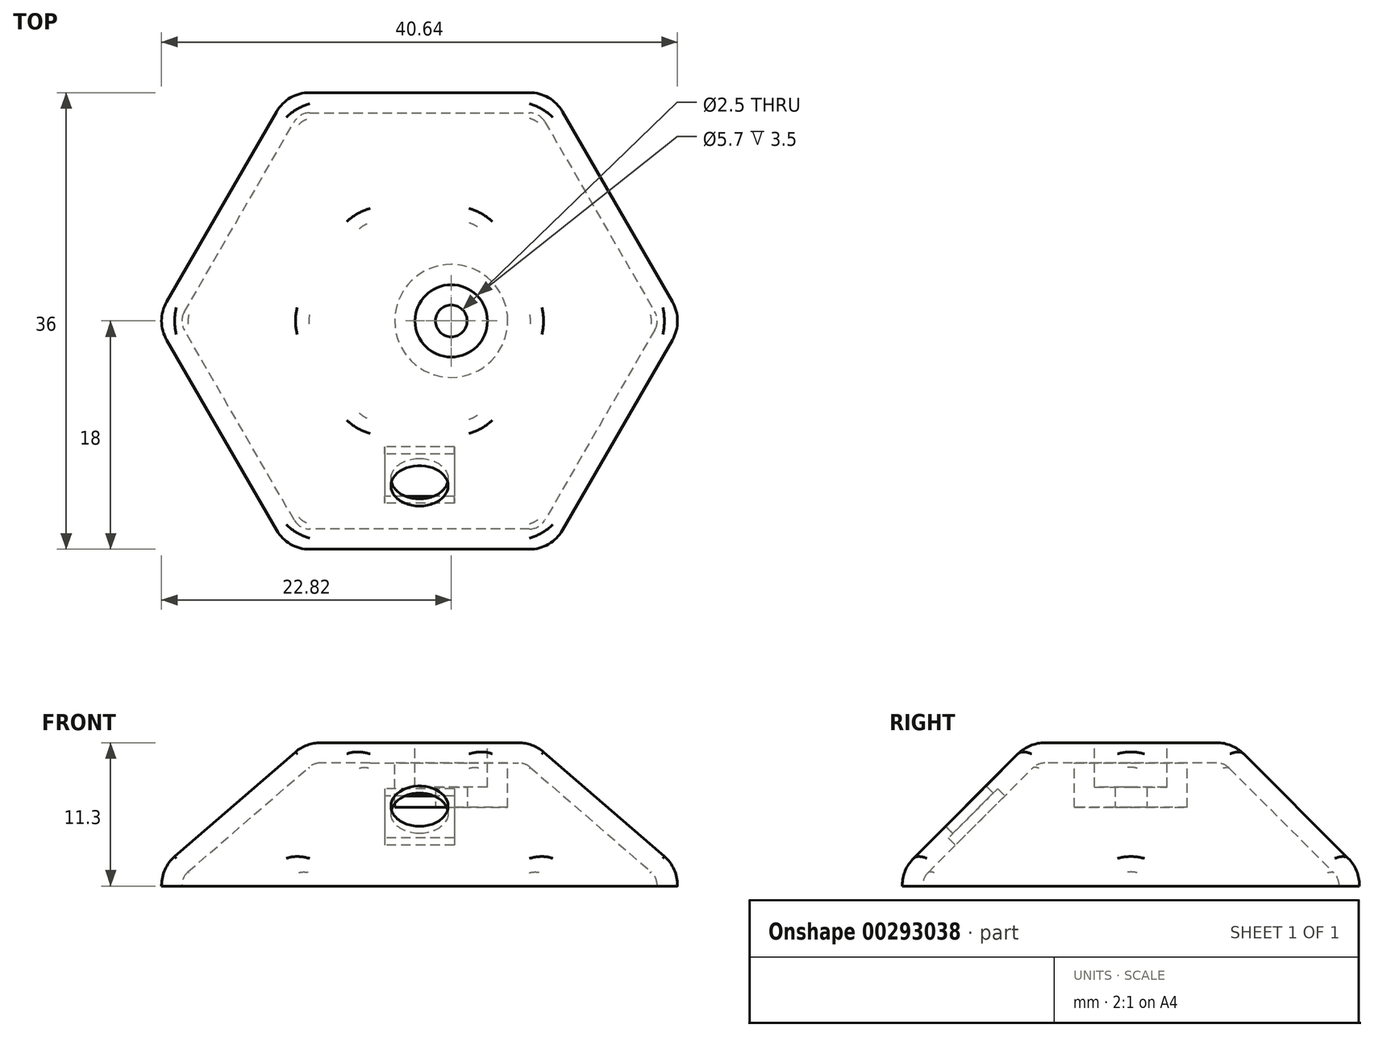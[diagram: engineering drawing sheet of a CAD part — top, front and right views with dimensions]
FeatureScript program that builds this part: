
annotation { "Feature Type Name" : "Feature", "Feature Type Description" : "" }
export const myFeature = defineFeature(function(context is Context, id is Id, definition is map)
    precondition{}
    {
        {
            var Q0;
            Q0=qCreatedBy(makeId("Top.planeOp"),FACE);
            var sketch = newSketch(context, id + "F0", { "sketchPlane" : qUnion([Q0])});
            skCircle(sketch, "E0.cCircle", {"center": v(0, 0) * mm, "radius": 18 * mm, "construction": true});
            skLineSegment(sketch, "E0.0", {"start": v(-10.4, 18) * mm, "end": v(10.4, 18) * mm});
            skLineSegment(sketch, "E0.1", {"start": v(10.4, 18) * mm, "end": v(20.78, 0) * mm});
            skLineSegment(sketch, "E0.2", {"start": v(20.78, 0) * mm, "end": v(10.4, -18) * mm});
            skLineSegment(sketch, "E0.3", {"start": v(10.4, -18) * mm, "end": v(-10.4, -18) * mm});
            skLineSegment(sketch, "E0.4", {"start": v(-10.4, -18) * mm, "end": v(-20.78, 0) * mm});
            skLineSegment(sketch, "E0.5", {"start": v(-20.78, 0) * mm, "end": v(-10.4, 18) * mm});
            skPoint(sketch, "E0.0.midPoint", {"position": v(0, 18) * mm});
            skSolve(sketch);
        }
        {
            var Q0;
            Q0=qSketchRegion(id+"F0",true);
            extrude(context, id + "F1", {"entities" : qUnion([Q0]), "endBound" : BoundingType.SYMMETRIC, "depth" : 36 * mm});
        }
        {
            var Q0;
            Q0=makeQuery(id+"F1.opExtrude","CAP_FACE",FACE,{"disambiguationData":[OSD([sQuery(id+"F0.wireOp",EDGE,"E0.0"),sQuery(id+"F0.wireOp",EDGE,"E0.1"),sQuery(id+"F0.wireOp",EDGE,"E0.2"),sQuery(id+"F0.wireOp",EDGE,"E0.3"),sQuery(id+"F0.wireOp",EDGE,"E0.4"),sQuery(id+"F0.wireOp",EDGE,"E0.5")])],"isStart":false});
            var Q1;
            Q1=makeQuery(id+"F1.opExtrude","CAP_FACE",FACE,{"disambiguationData":[OSD([sQuery(id+"F0.wireOp",EDGE,"E0.0"),sQuery(id+"F0.wireOp",EDGE,"E0.1"),sQuery(id+"F0.wireOp",EDGE,"E0.2"),sQuery(id+"F0.wireOp",EDGE,"E0.3"),sQuery(id+"F0.wireOp",EDGE,"E0.4"),sQuery(id+"F0.wireOp",EDGE,"E0.5")])],"isStart":true});
            chamfer(context, id + "F2", {"entities" : qUnion([Q0, Q1]), "chamferType" : ChamferType.OFFSET_ANGLE, "width" : 10 * mm, "oppositeDirection" : false, "angle" : 45 * degree, "tangentPropagation" : true});
        }
        {
            var Q0;
            Q0=makeQuery(id+"F1.opExtrude","CAP_FACE",FACE,{"disambiguationData":[OSD([sQuery(id+"F0.wireOp",EDGE,"E0.0"),sQuery(id+"F0.wireOp",EDGE,"E0.1"),sQuery(id+"F0.wireOp",EDGE,"E0.2"),sQuery(id+"F0.wireOp",EDGE,"E0.3"),sQuery(id+"F0.wireOp",EDGE,"E0.4"),sQuery(id+"F0.wireOp",EDGE,"E0.5")])],"isStart":true});
            var sketch = newSketch(context, id + "F3", { "sketchPlane" : qUnion([Q0])});
            skCircle(sketch, "E1", {"center": v(0, 0) * mm, "radius": 4.75 * mm});
            skSolve(sketch);
        }
        {
            var Q0;
            Q0=qSketchRegion(id+"F3",true);
            extrude(context, id + "F4", {"entities" : qUnion([Q0]), "operationType" : NewBodyOperationType.REMOVE, "oppositeDirection" : true, "depth" : 10 * mm});
        }
        {
            var Q0;
            Q0=makeQuery(id+"F4.boolean.opBoolean","COPY",FACE,{"derivedFrom":makeQuery(id+"F4.opExtrude","CAP_FACE",FACE,{"disambiguationData":[OSD([sQuery(id+"F3.wireOp",EDGE,"E1")])],"isStart":false})});
            var sketch = newSketch(context, id + "F5", { "sketchPlane" : qUnion([Q0])});
            skCircle(sketch, "E2", {"center": v(2.5, 0) * mm, "radius": 1.25 * mm});
            skSolve(sketch);
        }
        {
            var Q0;
            Q0=qSketchRegion(id+"F5",true);
            extrude(context, id + "F6", {"entities" : qUnion([Q0]), "operationType" : NewBodyOperationType.REMOVE, "oppositeDirection" : true, "depth" : 60 * mm});
        }
        {
            var Q0;
            {var subQ0=sQuery(id+"F0.wireOp",EDGE,"E0.3");Q0=makeQuery(id+"F2.opChamfer","BLEND_FACE",FACE,{"disambiguationData":[OSD([subQ0]),TDD([makeQuery(id+"F1.opExtrude","CAP_EDGE",EDGE,{"disambiguationData":[OSD([subQ0])],"isStart":false})])]});}
            var sketch = newSketch(context, id + "F7", { "sketchPlane" : qUnion([Q0])});
            skCircle(sketch, "E3", {"center": v(0, 0) * mm, "radius": 2.25 * mm});
            skSolve(sketch);
        }
        {
            var Q0;
            {var subQ0=sQuery(id+"F0.wireOp",EDGE,"E0.4");Q0=makeQuery(id+"F2.opChamfer","BLEND_EDGE",EDGE,{"blendedFrom":[makeQuery(id+"F1.opExtrude","CAP_EDGE",EDGE,{"disambiguationData":[OSD([subQ0])],"isStart":false}),makeQuery(id+"F1.opExtrude","SWEPT_FACE",FACE,{"disambiguationData":[OSD([subQ0])]})],"blendedInto":[makeQuery(id+"F1.opExtrude","SWEPT_FACE",FACE,{"disambiguationData":[OSD([subQ0])]})]});}
            var Q1;
            {var subQ0=sQuery(id+"F0.wireOp",EDGE,"E0.3");Q1=makeQuery(id+"F2.opChamfer","BLEND_EDGE",EDGE,{"blendedFrom":[makeQuery(id+"F1.opExtrude","CAP_EDGE",EDGE,{"disambiguationData":[OSD([subQ0])],"isStart":false}),makeQuery(id+"F1.opExtrude","SWEPT_FACE",FACE,{"disambiguationData":[OSD([subQ0])]})],"blendedInto":[makeQuery(id+"F1.opExtrude","SWEPT_FACE",FACE,{"disambiguationData":[OSD([subQ0])]})]});}
            var Q2;
            {var subQ0=sQuery(id+"F0.wireOp",EDGE,"E0.5");Q2=makeQuery(id+"F2.opChamfer","BLEND_EDGE",EDGE,{"blendedFrom":[makeQuery(id+"F1.opExtrude","CAP_EDGE",EDGE,{"disambiguationData":[OSD([subQ0])],"isStart":false}),makeQuery(id+"F1.opExtrude","SWEPT_FACE",FACE,{"disambiguationData":[OSD([subQ0])]})],"blendedInto":[makeQuery(id+"F1.opExtrude","SWEPT_FACE",FACE,{"disambiguationData":[OSD([subQ0])]})]});}
            var Q3;
            {var subQ0=sQuery(id+"F0.wireOp",EDGE,"E0.0");Q3=makeQuery(id+"F2.opChamfer","BLEND_EDGE",EDGE,{"blendedFrom":[makeQuery(id+"F1.opExtrude","CAP_EDGE",EDGE,{"disambiguationData":[OSD([subQ0])],"isStart":false}),makeQuery(id+"F1.opExtrude","SWEPT_FACE",FACE,{"disambiguationData":[OSD([subQ0])]})],"blendedInto":[makeQuery(id+"F1.opExtrude","SWEPT_FACE",FACE,{"disambiguationData":[OSD([subQ0])]})]});}
            var Q4;
            {var subQ0=sQuery(id+"F0.wireOp",EDGE,"E0.1");Q4=makeQuery(id+"F2.opChamfer","BLEND_EDGE",EDGE,{"blendedFrom":[makeQuery(id+"F1.opExtrude","CAP_EDGE",EDGE,{"disambiguationData":[OSD([subQ0])],"isStart":false}),makeQuery(id+"F1.opExtrude","SWEPT_FACE",FACE,{"disambiguationData":[OSD([subQ0])]})],"blendedInto":[makeQuery(id+"F1.opExtrude","SWEPT_FACE",FACE,{"disambiguationData":[OSD([subQ0])]})]});}
            var Q5;
            {var subQ0=sQuery(id+"F0.wireOp",EDGE,"E0.2");Q5=makeQuery(id+"F2.opChamfer","BLEND_EDGE",EDGE,{"blendedFrom":[makeQuery(id+"F1.opExtrude","CAP_EDGE",EDGE,{"disambiguationData":[OSD([subQ0])],"isStart":false}),makeQuery(id+"F1.opExtrude","SWEPT_FACE",FACE,{"disambiguationData":[OSD([subQ0])]})],"blendedInto":[makeQuery(id+"F1.opExtrude","SWEPT_FACE",FACE,{"disambiguationData":[OSD([subQ0])]})]});}
            var Q6;
            {var subQ0=sQuery(id+"F0.wireOp",EDGE,"E0.2");Q6=makeQuery(id+"F2.opChamfer","BLEND_EDGE",EDGE,{"blendedFrom":[makeQuery(id+"F1.opExtrude","CAP_EDGE",EDGE,{"disambiguationData":[OSD([subQ0])],"isStart":true}),makeQuery(id+"F1.opExtrude","SWEPT_FACE",FACE,{"disambiguationData":[OSD([subQ0])]})],"blendedInto":[makeQuery(id+"F1.opExtrude","SWEPT_FACE",FACE,{"disambiguationData":[OSD([subQ0])]})]});}
            var Q7;
            {var subQ0=sQuery(id+"F0.wireOp",EDGE,"E0.3");Q7=makeQuery(id+"F2.opChamfer","BLEND_EDGE",EDGE,{"blendedFrom":[makeQuery(id+"F1.opExtrude","CAP_EDGE",EDGE,{"disambiguationData":[OSD([subQ0])],"isStart":true}),makeQuery(id+"F1.opExtrude","SWEPT_FACE",FACE,{"disambiguationData":[OSD([subQ0])]})],"blendedInto":[makeQuery(id+"F1.opExtrude","SWEPT_FACE",FACE,{"disambiguationData":[OSD([subQ0])]})]});}
            var Q8;
            {var subQ0=sQuery(id+"F0.wireOp",EDGE,"E0.4");Q8=makeQuery(id+"F2.opChamfer","BLEND_EDGE",EDGE,{"blendedFrom":[makeQuery(id+"F1.opExtrude","CAP_EDGE",EDGE,{"disambiguationData":[OSD([subQ0])],"isStart":true}),makeQuery(id+"F1.opExtrude","SWEPT_FACE",FACE,{"disambiguationData":[OSD([subQ0])]})],"blendedInto":[makeQuery(id+"F1.opExtrude","SWEPT_FACE",FACE,{"disambiguationData":[OSD([subQ0])]})]});}
            var Q9;
            {var subQ0=sQuery(id+"F0.wireOp",EDGE,"E0.5");Q9=makeQuery(id+"F2.opChamfer","BLEND_EDGE",EDGE,{"blendedFrom":[makeQuery(id+"F1.opExtrude","CAP_EDGE",EDGE,{"disambiguationData":[OSD([subQ0])],"isStart":true}),makeQuery(id+"F1.opExtrude","SWEPT_FACE",FACE,{"disambiguationData":[OSD([subQ0])]})],"blendedInto":[makeQuery(id+"F1.opExtrude","SWEPT_FACE",FACE,{"disambiguationData":[OSD([subQ0])]})]});}
            var Q10;
            {var subQ0=sQuery(id+"F0.wireOp",EDGE,"E0.0");Q10=makeQuery(id+"F2.opChamfer","BLEND_EDGE",EDGE,{"blendedFrom":[makeQuery(id+"F1.opExtrude","CAP_EDGE",EDGE,{"disambiguationData":[OSD([subQ0])],"isStart":true}),makeQuery(id+"F1.opExtrude","SWEPT_FACE",FACE,{"disambiguationData":[OSD([subQ0])]})],"blendedInto":[makeQuery(id+"F1.opExtrude","SWEPT_FACE",FACE,{"disambiguationData":[OSD([subQ0])]})]});}
            var Q11;
            {var subQ0=sQuery(id+"F0.wireOp",EDGE,"E0.1");Q11=makeQuery(id+"F2.opChamfer","BLEND_EDGE",EDGE,{"blendedFrom":[makeQuery(id+"F1.opExtrude","CAP_EDGE",EDGE,{"disambiguationData":[OSD([subQ0])],"isStart":true}),makeQuery(id+"F1.opExtrude","SWEPT_FACE",FACE,{"disambiguationData":[OSD([subQ0])]})],"blendedInto":[makeQuery(id+"F1.opExtrude","SWEPT_FACE",FACE,{"disambiguationData":[OSD([subQ0])]})]});}
            fillet(context, id + "F8", {"entities" : qUnion([Q0, Q1, Q2, Q3, Q4, Q5, Q6, Q7, Q8, Q9, Q10, Q11]), "radius" : 3 * mm, "tangentPropagation" : true, "allowEdgeOverflow" : false});
        }
        {
            var Q0;
            Q0=makeQuery(id+"F2.opChamfer","BLEND_EDGE",EDGE,{"blendedFrom":[makeQuery(id+"F1.opExtrude","CAP_EDGE",EDGE,{"disambiguationData":[OSD([sQuery(id+"F0.wireOp",EDGE,"E0.4")])],"isStart":true}),makeQuery(id+"F1.opExtrude","CAP_EDGE",EDGE,{"disambiguationData":[OSD([sQuery(id+"F0.wireOp",EDGE,"E0.5")])],"isStart":true})],"blendedInto":[]});
            var Q1;
            Q1=makeQuery(id+"F2.opChamfer","BLEND_EDGE",EDGE,{"blendedFrom":[makeQuery(id+"F1.opExtrude","CAP_EDGE",EDGE,{"disambiguationData":[OSD([sQuery(id+"F0.wireOp",EDGE,"E0.0")])],"isStart":true}),makeQuery(id+"F1.opExtrude","CAP_EDGE",EDGE,{"disambiguationData":[OSD([sQuery(id+"F0.wireOp",EDGE,"E0.5")])],"isStart":true})],"blendedInto":[]});
            var Q2;
            {var subQ0=sQuery(id+"F0.wireOp",EDGE,"E0.5");Q2=makeQuery(id+"F2.opChamfer","BLEND_EDGE",EDGE,{"blendedFrom":[makeQuery(id+"F1.opExtrude","CAP_EDGE",EDGE,{"disambiguationData":[OSD([subQ0])],"isStart":true}),makeQuery(id+"F1.opExtrude","CAP_FACE",FACE,{"disambiguationData":[OSD([sQuery(id+"F0.wireOp",EDGE,"E0.0"),sQuery(id+"F0.wireOp",EDGE,"E0.1"),sQuery(id+"F0.wireOp",EDGE,"E0.2"),sQuery(id+"F0.wireOp",EDGE,"E0.3"),sQuery(id+"F0.wireOp",EDGE,"E0.4"),subQ0])],"isStart":true})],"blendedInto":[makeQuery(id+"F1.opExtrude","CAP_FACE",FACE,{"disambiguationData":[OSD([sQuery(id+"F0.wireOp",EDGE,"E0.0"),sQuery(id+"F0.wireOp",EDGE,"E0.1"),sQuery(id+"F0.wireOp",EDGE,"E0.2"),sQuery(id+"F0.wireOp",EDGE,"E0.3"),sQuery(id+"F0.wireOp",EDGE,"E0.4"),subQ0])],"isStart":true})]});}
            var Q3;
            {var subQ0=sQuery(id+"F0.wireOp",EDGE,"E0.4");Q3=makeQuery(id+"F2.opChamfer","BLEND_EDGE",EDGE,{"blendedFrom":[makeQuery(id+"F1.opExtrude","CAP_EDGE",EDGE,{"disambiguationData":[OSD([subQ0])],"isStart":true}),makeQuery(id+"F1.opExtrude","CAP_FACE",FACE,{"disambiguationData":[OSD([sQuery(id+"F0.wireOp",EDGE,"E0.0"),sQuery(id+"F0.wireOp",EDGE,"E0.1"),sQuery(id+"F0.wireOp",EDGE,"E0.2"),sQuery(id+"F0.wireOp",EDGE,"E0.3"),subQ0,sQuery(id+"F0.wireOp",EDGE,"E0.5")])],"isStart":true})],"blendedInto":[makeQuery(id+"F1.opExtrude","CAP_FACE",FACE,{"disambiguationData":[OSD([sQuery(id+"F0.wireOp",EDGE,"E0.0"),sQuery(id+"F0.wireOp",EDGE,"E0.1"),sQuery(id+"F0.wireOp",EDGE,"E0.2"),sQuery(id+"F0.wireOp",EDGE,"E0.3"),subQ0,sQuery(id+"F0.wireOp",EDGE,"E0.5")])],"isStart":true})]});}
            var Q4;
            Q4=makeQuery(id+"F2.opChamfer","BLEND_EDGE",EDGE,{"blendedFrom":[makeQuery(id+"F1.opExtrude","CAP_EDGE",EDGE,{"disambiguationData":[OSD([sQuery(id+"F0.wireOp",EDGE,"E0.3")])],"isStart":true}),makeQuery(id+"F1.opExtrude","CAP_EDGE",EDGE,{"disambiguationData":[OSD([sQuery(id+"F0.wireOp",EDGE,"E0.4")])],"isStart":true})],"blendedInto":[]});
            var Q5;
            {var subQ0=sQuery(id+"F0.wireOp",EDGE,"E0.3");Q5=makeQuery(id+"F2.opChamfer","BLEND_EDGE",EDGE,{"blendedFrom":[makeQuery(id+"F1.opExtrude","CAP_EDGE",EDGE,{"disambiguationData":[OSD([subQ0])],"isStart":true}),makeQuery(id+"F1.opExtrude","CAP_FACE",FACE,{"disambiguationData":[OSD([sQuery(id+"F0.wireOp",EDGE,"E0.0"),sQuery(id+"F0.wireOp",EDGE,"E0.1"),sQuery(id+"F0.wireOp",EDGE,"E0.2"),subQ0,sQuery(id+"F0.wireOp",EDGE,"E0.4"),sQuery(id+"F0.wireOp",EDGE,"E0.5")])],"isStart":true})],"blendedInto":[makeQuery(id+"F1.opExtrude","CAP_FACE",FACE,{"disambiguationData":[OSD([sQuery(id+"F0.wireOp",EDGE,"E0.0"),sQuery(id+"F0.wireOp",EDGE,"E0.1"),sQuery(id+"F0.wireOp",EDGE,"E0.2"),subQ0,sQuery(id+"F0.wireOp",EDGE,"E0.4"),sQuery(id+"F0.wireOp",EDGE,"E0.5")])],"isStart":true})]});}
            var Q6;
            {var subQ0=sQuery(id+"F0.wireOp",EDGE,"E0.0");Q6=makeQuery(id+"F2.opChamfer","BLEND_EDGE",EDGE,{"blendedFrom":[makeQuery(id+"F1.opExtrude","CAP_EDGE",EDGE,{"disambiguationData":[OSD([subQ0])],"isStart":true}),makeQuery(id+"F1.opExtrude","CAP_FACE",FACE,{"disambiguationData":[OSD([subQ0,sQuery(id+"F0.wireOp",EDGE,"E0.1"),sQuery(id+"F0.wireOp",EDGE,"E0.2"),sQuery(id+"F0.wireOp",EDGE,"E0.3"),sQuery(id+"F0.wireOp",EDGE,"E0.4"),sQuery(id+"F0.wireOp",EDGE,"E0.5")])],"isStart":true})],"blendedInto":[makeQuery(id+"F1.opExtrude","CAP_FACE",FACE,{"disambiguationData":[OSD([subQ0,sQuery(id+"F0.wireOp",EDGE,"E0.1"),sQuery(id+"F0.wireOp",EDGE,"E0.2"),sQuery(id+"F0.wireOp",EDGE,"E0.3"),sQuery(id+"F0.wireOp",EDGE,"E0.4"),sQuery(id+"F0.wireOp",EDGE,"E0.5")])],"isStart":true})]});}
            var Q7;
            Q7=makeQuery(id+"F2.opChamfer","BLEND_EDGE",EDGE,{"blendedFrom":[makeQuery(id+"F1.opExtrude","CAP_EDGE",EDGE,{"disambiguationData":[OSD([sQuery(id+"F0.wireOp",EDGE,"E0.0")])],"isStart":true}),makeQuery(id+"F1.opExtrude","CAP_EDGE",EDGE,{"disambiguationData":[OSD([sQuery(id+"F0.wireOp",EDGE,"E0.1")])],"isStart":true})],"blendedInto":[]});
            var Q8;
            Q8=makeQuery(id+"F2.opChamfer","BLEND_EDGE",EDGE,{"blendedFrom":[makeQuery(id+"F1.opExtrude","CAP_EDGE",EDGE,{"disambiguationData":[OSD([sQuery(id+"F0.wireOp",EDGE,"E0.2")])],"isStart":true}),makeQuery(id+"F1.opExtrude","CAP_EDGE",EDGE,{"disambiguationData":[OSD([sQuery(id+"F0.wireOp",EDGE,"E0.3")])],"isStart":true})],"blendedInto":[]});
            var Q9;
            {var subQ0=sQuery(id+"F0.wireOp",EDGE,"E0.2");Q9=makeQuery(id+"F2.opChamfer","BLEND_EDGE",EDGE,{"blendedFrom":[makeQuery(id+"F1.opExtrude","CAP_EDGE",EDGE,{"disambiguationData":[OSD([subQ0])],"isStart":true}),makeQuery(id+"F1.opExtrude","CAP_FACE",FACE,{"disambiguationData":[OSD([sQuery(id+"F0.wireOp",EDGE,"E0.0"),sQuery(id+"F0.wireOp",EDGE,"E0.1"),subQ0,sQuery(id+"F0.wireOp",EDGE,"E0.3"),sQuery(id+"F0.wireOp",EDGE,"E0.4"),sQuery(id+"F0.wireOp",EDGE,"E0.5")])],"isStart":true})],"blendedInto":[makeQuery(id+"F1.opExtrude","CAP_FACE",FACE,{"disambiguationData":[OSD([sQuery(id+"F0.wireOp",EDGE,"E0.0"),sQuery(id+"F0.wireOp",EDGE,"E0.1"),subQ0,sQuery(id+"F0.wireOp",EDGE,"E0.3"),sQuery(id+"F0.wireOp",EDGE,"E0.4"),sQuery(id+"F0.wireOp",EDGE,"E0.5")])],"isStart":true})]});}
            var Q10;
            Q10=makeQuery(id+"F2.opChamfer","BLEND_EDGE",EDGE,{"blendedFrom":[makeQuery(id+"F1.opExtrude","CAP_EDGE",EDGE,{"disambiguationData":[OSD([sQuery(id+"F0.wireOp",EDGE,"E0.1")])],"isStart":true}),makeQuery(id+"F1.opExtrude","CAP_EDGE",EDGE,{"disambiguationData":[OSD([sQuery(id+"F0.wireOp",EDGE,"E0.2")])],"isStart":true})],"blendedInto":[]});
            var Q11;
            {var subQ0=sQuery(id+"F0.wireOp",EDGE,"E0.1");Q11=makeQuery(id+"F2.opChamfer","BLEND_EDGE",EDGE,{"blendedFrom":[makeQuery(id+"F1.opExtrude","CAP_EDGE",EDGE,{"disambiguationData":[OSD([subQ0])],"isStart":true}),makeQuery(id+"F1.opExtrude","CAP_FACE",FACE,{"disambiguationData":[OSD([sQuery(id+"F0.wireOp",EDGE,"E0.0"),subQ0,sQuery(id+"F0.wireOp",EDGE,"E0.2"),sQuery(id+"F0.wireOp",EDGE,"E0.3"),sQuery(id+"F0.wireOp",EDGE,"E0.4"),sQuery(id+"F0.wireOp",EDGE,"E0.5")])],"isStart":true})],"blendedInto":[makeQuery(id+"F1.opExtrude","CAP_FACE",FACE,{"disambiguationData":[OSD([sQuery(id+"F0.wireOp",EDGE,"E0.0"),subQ0,sQuery(id+"F0.wireOp",EDGE,"E0.2"),sQuery(id+"F0.wireOp",EDGE,"E0.3"),sQuery(id+"F0.wireOp",EDGE,"E0.4"),sQuery(id+"F0.wireOp",EDGE,"E0.5")])],"isStart":true})]});}
            fillet(context, id + "F9", {"entities" : qUnion([Q0, Q1, Q2, Q3, Q4, Q5, Q6, Q7, Q8, Q9, Q10, Q11]), "radius" : 3 * mm, "tangentPropagation" : true, "allowEdgeOverflow" : false});
        }
        {
            var Q0;
            {var subQ0=sQuery(id+"F0.wireOp",EDGE,"E0.5");Q0=makeQuery(id+"F2.opChamfer","BLEND_EDGE",EDGE,{"blendedFrom":[makeQuery(id+"F1.opExtrude","CAP_EDGE",EDGE,{"disambiguationData":[OSD([subQ0])],"isStart":false}),makeQuery(id+"F1.opExtrude","CAP_FACE",FACE,{"disambiguationData":[OSD([sQuery(id+"F0.wireOp",EDGE,"E0.0"),sQuery(id+"F0.wireOp",EDGE,"E0.1"),sQuery(id+"F0.wireOp",EDGE,"E0.2"),sQuery(id+"F0.wireOp",EDGE,"E0.3"),sQuery(id+"F0.wireOp",EDGE,"E0.4"),subQ0])],"isStart":false})],"blendedInto":[makeQuery(id+"F1.opExtrude","CAP_FACE",FACE,{"disambiguationData":[OSD([sQuery(id+"F0.wireOp",EDGE,"E0.0"),sQuery(id+"F0.wireOp",EDGE,"E0.1"),sQuery(id+"F0.wireOp",EDGE,"E0.2"),sQuery(id+"F0.wireOp",EDGE,"E0.3"),sQuery(id+"F0.wireOp",EDGE,"E0.4"),subQ0])],"isStart":false})]});}
            var Q1;
            {var subQ0=sQuery(id+"F0.wireOp",EDGE,"E0.4");Q1=makeQuery(id+"F2.opChamfer","BLEND_EDGE",EDGE,{"blendedFrom":[makeQuery(id+"F1.opExtrude","CAP_EDGE",EDGE,{"disambiguationData":[OSD([subQ0])],"isStart":false}),makeQuery(id+"F1.opExtrude","CAP_FACE",FACE,{"disambiguationData":[OSD([sQuery(id+"F0.wireOp",EDGE,"E0.0"),sQuery(id+"F0.wireOp",EDGE,"E0.1"),sQuery(id+"F0.wireOp",EDGE,"E0.2"),sQuery(id+"F0.wireOp",EDGE,"E0.3"),subQ0,sQuery(id+"F0.wireOp",EDGE,"E0.5")])],"isStart":false})],"blendedInto":[makeQuery(id+"F1.opExtrude","CAP_FACE",FACE,{"disambiguationData":[OSD([sQuery(id+"F0.wireOp",EDGE,"E0.0"),sQuery(id+"F0.wireOp",EDGE,"E0.1"),sQuery(id+"F0.wireOp",EDGE,"E0.2"),sQuery(id+"F0.wireOp",EDGE,"E0.3"),subQ0,sQuery(id+"F0.wireOp",EDGE,"E0.5")])],"isStart":false})]});}
            fillet(context, id + "F10", {"entities" : qUnion([Q0, Q1]), "radius" : 3 * mm, "tangentPropagation" : true, "allowEdgeOverflow" : false});
        }
        {
            var Q0;
            Q0=makeQuery(id+"F1.opExtrude","CAP_FACE",FACE,{"disambiguationData":[OSD([sQuery(id+"F0.wireOp",EDGE,"E0.0"),sQuery(id+"F0.wireOp",EDGE,"E0.1"),sQuery(id+"F0.wireOp",EDGE,"E0.2"),sQuery(id+"F0.wireOp",EDGE,"E0.3"),sQuery(id+"F0.wireOp",EDGE,"E0.4"),sQuery(id+"F0.wireOp",EDGE,"E0.5")])],"isStart":false});
            var sketch = newSketch(context, id + "F11", { "sketchPlane" : qUnion([Q0])});
            skCircle(sketch, "E4", {"center": v(2.5, 0) * mm, "radius": 2.85 * mm});
            skSolve(sketch);
        }
        {
            var Q0;
            Q0=qSketchRegion(id+"F11",true);
            extrude(context, id + "F12", {"entities" : qUnion([Q0]), "operationType" : NewBodyOperationType.REMOVE, "oppositeDirection" : true, "depth" : 3.5 * mm});
        }
        {
            var Q0;
            Q0=qCreatedBy(makeId("Top.planeOp"),FACE);
            cPlane(context, id + "F13", {"entities" : qUnion([Q0]), "cplaneType" : CPlaneType.OFFSET, "offset" : 6.7 * mm, "width" : 150 * mm, "height" : 150 * mm});
        }
        {
            var Q0;
            Q0=qCreatedBy(id+"F13.planeOp",FACE);
            var sketch = newSketch(context, id + "F14", { "sketchPlane" : qUnion([Q0])});
            skLineSegment(sketch, "E5.bottom", {"start": v(-35.89, 28.17) * mm, "end": v(42.4, 28.17) * mm});
            skLineSegment(sketch, "E5.top", {"start": v(-35.89, -30.96) * mm, "end": v(42.4, -30.96) * mm});
            skLineSegment(sketch, "E5.left", {"start": v(-35.89, 28.17) * mm, "end": v(-35.89, -30.96) * mm});
            skLineSegment(sketch, "E5.right", {"start": v(42.4, 28.17) * mm, "end": v(42.4, -30.96) * mm});
            skSolve(sketch);
        }
        {
            var Q0;
            Q0 = qSketchRegion(id + "F14", true);
            extrude(context, id + "F15", {"entities" : qUnion([Q0]), "operationType" : NewBodyOperationType.REMOVE, "oppositeDirection" : true, "depth" : 25 * mm});
        }
        {
            var Q0;
            Q0=makeQuery(id+"F15.boolean.opBoolean","COPY",FACE,{"derivedFrom":makeQuery(id+"F15.opExtrude","CAP_FACE",FACE,{"disambiguationData":[OSD([sQuery(id+"F14.wireOp",EDGE,"E5.bottom"),sQuery(id+"F14.wireOp",EDGE,"E5.top"),sQuery(id+"F14.wireOp",EDGE,"E5.left"),sQuery(id+"F14.wireOp",EDGE,"E5.right")])],"isStart":true})});
            shell(context, id + "F16", {"entities" : qUnion([Q0]), "thickness" : 1.6 * mm});
        }
        {
            var Q0;
            {var subQ0=sQuery(id+"F11.wireOp",EDGE,"E4");Q0=makeQuery(id+"F16.opShell","OFFSET_FACE",FACE,{"disambiguationData":[OSD([subQ0]),TDD([makeQuery(id+"F12.boolean.opBoolean","COPY",FACE,{"derivedFrom":makeQuery(id+"F12.opExtrude","CAP_FACE",FACE,{"disambiguationData":[OSD([subQ0])],"isStart":false})})])]});}
            var sketch = newSketch(context, id + "F17", { "sketchPlane" : qUnion([Q0])});
            skCircle(sketch, "E6.0", {"center": v(2.5, 0) * mm, "radius": 4.45 * mm});
            skSolve(sketch);
        }
        {
            var Q0;
            Q0 = qSketchRegion(id + "F17", true);
            extrude(context, id + "F18", {"entities" : qUnion([Q0]), "operationType" : NewBodyOperationType.REMOVE, "depth" : 25 * mm});
        }
        {
            var Q0;
            Q0=qCreatedBy(makeId("Front.planeOp"),FACE);
            var sketch = newSketch(context, id + "F19", { "sketchPlane" : qUnion([Q0])});
            skLineSegment(sketch, "E7", {"start": v(0, 38.58) * mm, "end": v(0, -40.26) * mm, "construction": true});
            skSolve(sketch);
        }
        {
            var Q0;
            Q0 = qSketchRegion(id + "F7", true);
            extrude(context, id + "F20", {"entities" : qUnion([Q0]), "operationType" : NewBodyOperationType.REMOVE, "oppositeDirection" : true, "depth" : 10 * mm});
        }
        {
            var Q0;
            {var subQ0=sQuery(id+"F0.wireOp",EDGE,"E0.3");Q0=makeQuery(id+"F16.opShell","OFFSET_FACE",FACE,{"disambiguationData":[OSD([subQ0]),TDD([makeQuery(id+"F2.opChamfer","BLEND_FACE",FACE,{"disambiguationData":[OSD([subQ0]),TDD([makeQuery(id+"F1.opExtrude","CAP_EDGE",EDGE,{"disambiguationData":[OSD([subQ0])],"isStart":false})])]})])]});}
            var sketch = newSketch(context, id + "F21", { "sketchPlane" : qUnion([Q0])});
            skLineSegment(sketch, "E8.bottom", {"start": v(-2.75, 2.75) * mm, "end": v(2.75, 2.75) * mm});
            skLineSegment(sketch, "E8.top", {"start": v(-2.75, -2.75) * mm, "end": v(2.75, -2.75) * mm});
            skLineSegment(sketch, "E8.left", {"start": v(-2.75, 2.75) * mm, "end": v(-2.75, -2.75) * mm});
            skLineSegment(sketch, "E8.right", {"start": v(2.75, 2.75) * mm, "end": v(2.75, -2.75) * mm});
            skSolve(sketch);
        }
        {
            var Q0;
            Q0 = qSketchRegion(id + "F21", true);
            extrude(context, id + "F22", {"entities" : qUnion([Q0]), "operationType" : NewBodyOperationType.REMOVE, "oppositeDirection" : true, "depth" : 0.8 * mm});
        }
        {
            var Q0;
            Q0=qCreatedBy(makeId("Front.planeOp"),FACE);
            var sketch = newSketch(context, id + "F23", { "sketchPlane" : qUnion([Q0])});
            skLineSegment(sketch, "E9", {"start": v(0, 45.48) * mm, "end": v(0, -41.16) * mm, "construction": true});
            skSolve(sketch);
        }
    });
